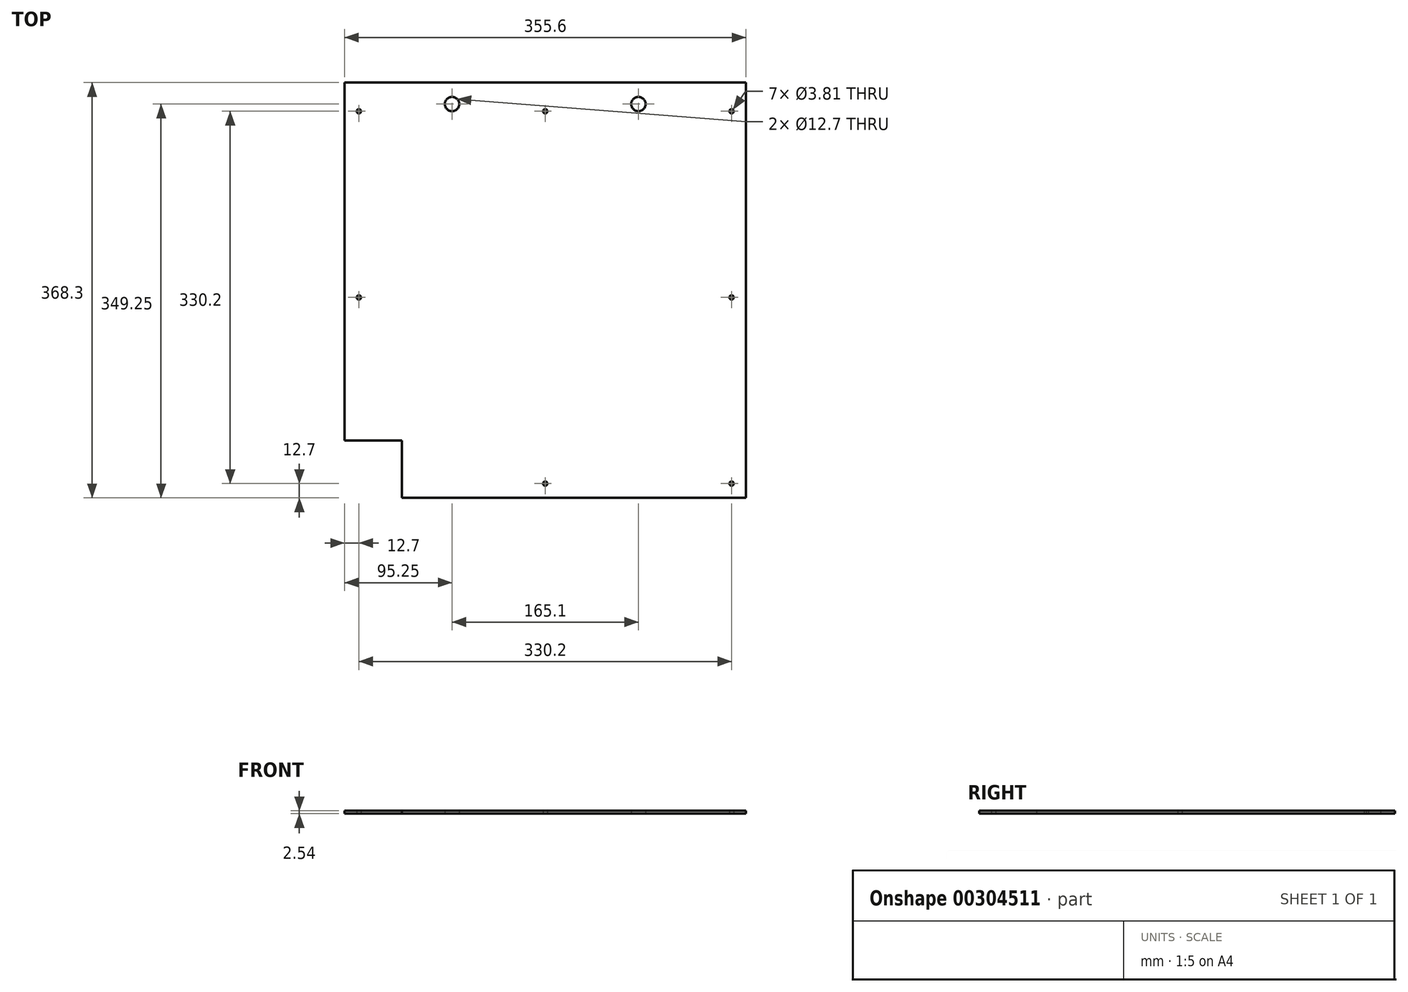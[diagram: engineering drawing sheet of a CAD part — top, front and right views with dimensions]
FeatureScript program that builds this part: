
annotation { "Feature Type Name" : "Feature", "Feature Type Description" : "" }
export const myFeature = defineFeature(function(context is Context, id is Id, definition is map)
    precondition{}
    {
        {
            var Q0;
            Q0=qCreatedBy(makeId("Top.planeOp"),FACE);
            var sketch = newSketch(context, id + "F0", { "sketchPlane" : qUnion([Q0])});
            skLineSegment(sketch, "E0.bottom", {"start": v(177.8, -177.8) * mm, "end": v(-127, -177.8) * mm});
            skLineSegment(sketch, "E0.top", {"start": v(177.8, 190.5) * mm, "end": v(-177.8, 190.5) * mm});
            skLineSegment(sketch, "E0.left", {"start": v(177.8, -177.8) * mm, "end": v(177.8, 190.5) * mm});
            skLineSegment(sketch, "E0.right", {"start": v(-177.8, -127) * mm, "end": v(-177.8, 190.5) * mm});
            skPoint(sketch, "E0.middle", {"position": v(0, 0) * mm});
            skLineSegment(sketch, "E1.top", {"start": v(-177.8, -127) * mm, "end": v(-127, -127) * mm});
            skLineSegment(sketch, "E1.right", {"start": v(-127, -177.8) * mm, "end": v(-127, -127) * mm});
            skCircle(sketch, "E2", {"center": v(-165.1, 0) * mm, "radius": 1.9 * mm});
            skCircle(sketch, "E3", {"center": v(-165.1, 165.1) * mm, "radius": 1.9 * mm});
            skCircle(sketch, "E4", {"center": v(165.1, 165.1) * mm, "radius": 1.9 * mm});
            skCircle(sketch, "E5", {"center": v(0, 165.1) * mm, "radius": 1.9 * mm});
            skCircle(sketch, "E6", {"center": v(0, -165.1) * mm, "radius": 1.9 * mm});
            skCircle(sketch, "E7", {"center": v(165.1, -165.1) * mm, "radius": 1.9 * mm});
            skCircle(sketch, "E8", {"center": v(165.1, 0) * mm, "radius": 1.9 * mm});
            skLineSegment(sketch, "E9.bottom", {"start": v(165.1, 165.1) * mm, "end": v(-165.1, 165.1) * mm, "construction": true});
            skLineSegment(sketch, "E9.top", {"start": v(165.1, -165.1) * mm, "end": v(-165.1, -165.1) * mm, "construction": true});
            skLineSegment(sketch, "E9.left", {"start": v(165.1, 165.1) * mm, "end": v(165.1, -165.1) * mm, "construction": true});
            skLineSegment(sketch, "E9.right", {"start": v(-165.1, 165.1) * mm, "end": v(-165.1, -165.1) * mm, "construction": true});
            skLineSegment(sketch, "E10", {"start": v(0, 165.1) * mm, "end": v(-82.55, 165.1) * mm, "construction": true});
            skLineSegment(sketch, "E11", {"start": v(0, 165.1) * mm, "end": v(82.55, 165.1) * mm, "construction": true});
            skLineSegment(sketch, "E12", {"start": v(-82.55, 165.1) * mm, "end": v(-82.55, 171.45) * mm, "construction": true});
            skLineSegment(sketch, "E13", {"start": v(82.55, 165.1) * mm, "end": v(82.55, 171.45) * mm, "construction": true});
            skCircle(sketch, "E14", {"center": v(-82.55, 171.45) * mm, "radius": 6.35 * mm});
            skCircle(sketch, "E15", {"center": v(82.55, 171.45) * mm, "radius": 6.35 * mm});
            skSolve(sketch);
        }
        {
            var Q0;
            Q0=makeQuery(id+"F0.imprint","IMPRINT",FACE,{"disambiguationData":[TD([[makeQuery(id+"F0.imprint","IMPRINT",EDGE,{"derivedFrom":sQuery(id+"F0.wireOp",EDGE,"E0.bottom")}),-1.0]])]});
            extrude(context, id + "F1", {"entities" : qUnion([Q0]), "depth" : 2.54 * mm});
        }
    });
